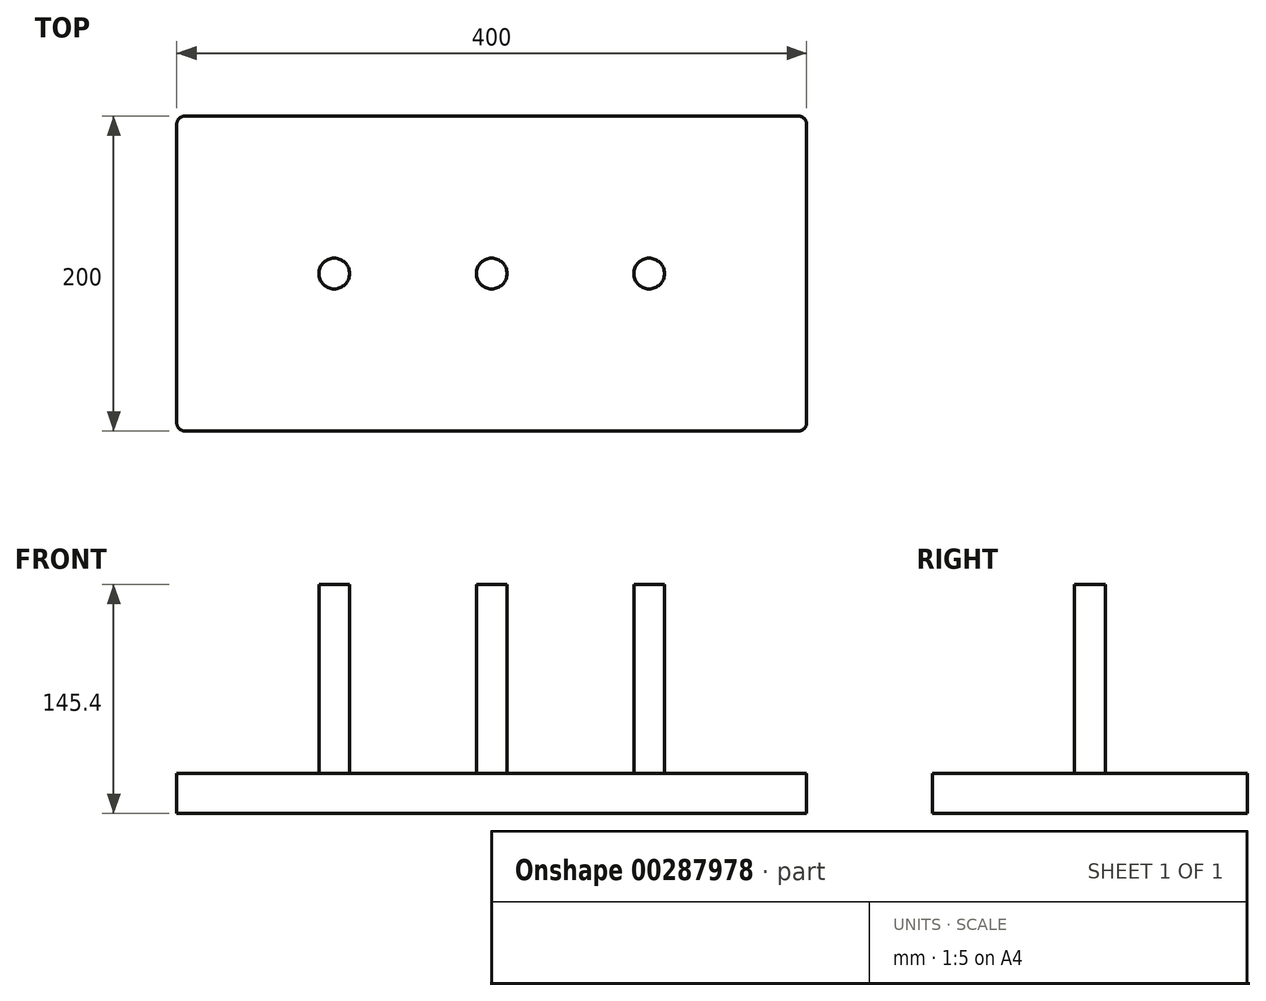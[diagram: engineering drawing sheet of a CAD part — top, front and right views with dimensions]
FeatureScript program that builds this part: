
annotation { "Feature Type Name" : "Feature", "Feature Type Description" : "" }
export const myFeature = defineFeature(function(context is Context, id is Id, definition is map)
    precondition{}
    {
        {
            var Q0;
            Q0=qCreatedBy(makeId("Top.planeOp"),FACE);
            var sketch = newSketch(context, id + "F0", { "sketchPlane" : qUnion([Q0])});
            skLineSegment(sketch, "E0.bottom", {"start": v(-200, 100) * mm, "end": v(200, 100) * mm});
            skLineSegment(sketch, "E0.top", {"start": v(-200, -100) * mm, "end": v(200, -100) * mm});
            skLineSegment(sketch, "E0.left", {"start": v(-200, 100) * mm, "end": v(-200, -100) * mm});
            skLineSegment(sketch, "E0.right", {"start": v(200, 100) * mm, "end": v(200, -100) * mm});
            skPoint(sketch, "E0.middle", {"position": v(0, 0) * mm});
            skSolve(sketch);
        }
        {
            var Q0;
            Q0=makeQuery(id+"F0.imprint","IMPRINT",FACE,{"disambiguationData":[TD([[makeQuery(id+"F0.imprint","IMPRINT",EDGE,{"derivedFrom":sQuery(id+"F0.wireOp",EDGE,"E0.bottom")}),-1.0]])]});
            extrude(context, id + "F1", {"entities" : qUnion([Q0]), "depth" : 25.4 * mm});
        }
        {
            var Q0;
            Q0=makeQuery(id+"F1.opExtrude","SWEPT_EDGE",EDGE,{"disambiguationData":[OSD([sQuery(id+"F0.wireOp",EDGE,"E0.bottom"),sQuery(id+"F0.wireOp",EDGE,"E0.right")])]});
            var Q1;
            Q1=makeQuery(id+"F1.opExtrude","SWEPT_EDGE",EDGE,{"disambiguationData":[OSD([sQuery(id+"F0.wireOp",EDGE,"E0.top"),sQuery(id+"F0.wireOp",EDGE,"E0.right")])]});
            var Q2;
            Q2=makeQuery(id+"F1.opExtrude","SWEPT_EDGE",EDGE,{"disambiguationData":[OSD([sQuery(id+"F0.wireOp",EDGE,"E0.bottom"),sQuery(id+"F0.wireOp",EDGE,"E0.left")])]});
            var Q3;
            Q3=makeQuery(id+"F1.opExtrude","SWEPT_EDGE",EDGE,{"disambiguationData":[OSD([sQuery(id+"F0.wireOp",EDGE,"E0.top"),sQuery(id+"F0.wireOp",EDGE,"E0.left")])]});
            fillet(context, id + "F2", {"entities" : qUnion([Q0, Q1, Q2, Q3]), "radius" : 5.08 * mm, "tangentPropagation" : true, "allowEdgeOverflow" : false});
        }
        {
            var Q0;
            Q0=makeQuery(id+"F1.opExtrude","CAP_FACE",FACE,{"disambiguationData":[OSD([sQuery(id+"F0.wireOp",EDGE,"E0.bottom"),sQuery(id+"F0.wireOp",EDGE,"E0.top"),sQuery(id+"F0.wireOp",EDGE,"E0.left"),sQuery(id+"F0.wireOp",EDGE,"E0.right")])],"isStart":false});
            var sketch = newSketch(context, id + "F3", { "sketchPlane" : qUnion([Q0])});
            skCircle(sketch, "E1", {"center": v(-100, 0) * mm, "radius": 9.75 * mm});
            skCircle(sketch, "E2", {"center": v(0, 0) * mm, "radius": 9.75 * mm});
            skCircle(sketch, "E3", {"center": v(100, 0) * mm, "radius": 9.75 * mm});
            skSolve(sketch);
        }
        {
            var Q0;
            Q0=qSketchRegion(id+"F3",true);
            extrude(context, id + "F4", {"entities" : qUnion([Q0]), "operationType" : NewBodyOperationType.ADD, "depth" : 120 * mm});
        }
    });
